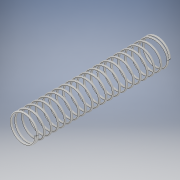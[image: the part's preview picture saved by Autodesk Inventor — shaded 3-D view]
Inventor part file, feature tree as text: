
AUTODESK INVENTOR PART (.ipt)
format: ipt  version: 2018 (Build 220112000, 112)  size: 927,232 bytes
history: native  units: in
note: dims shown in document units (in); Inventor stores cm internally (conversion verified against a paired STEP export)
features: sweep x1
ambient origin geometry x8: Origin, YZ Plane, XZ Plane, XY Plane, X Axis, Y Axis, Z Axis, Center Point
bodies: Solid1 (feature_tree)
feature tree (1):
  sweep  "Sweep1"
